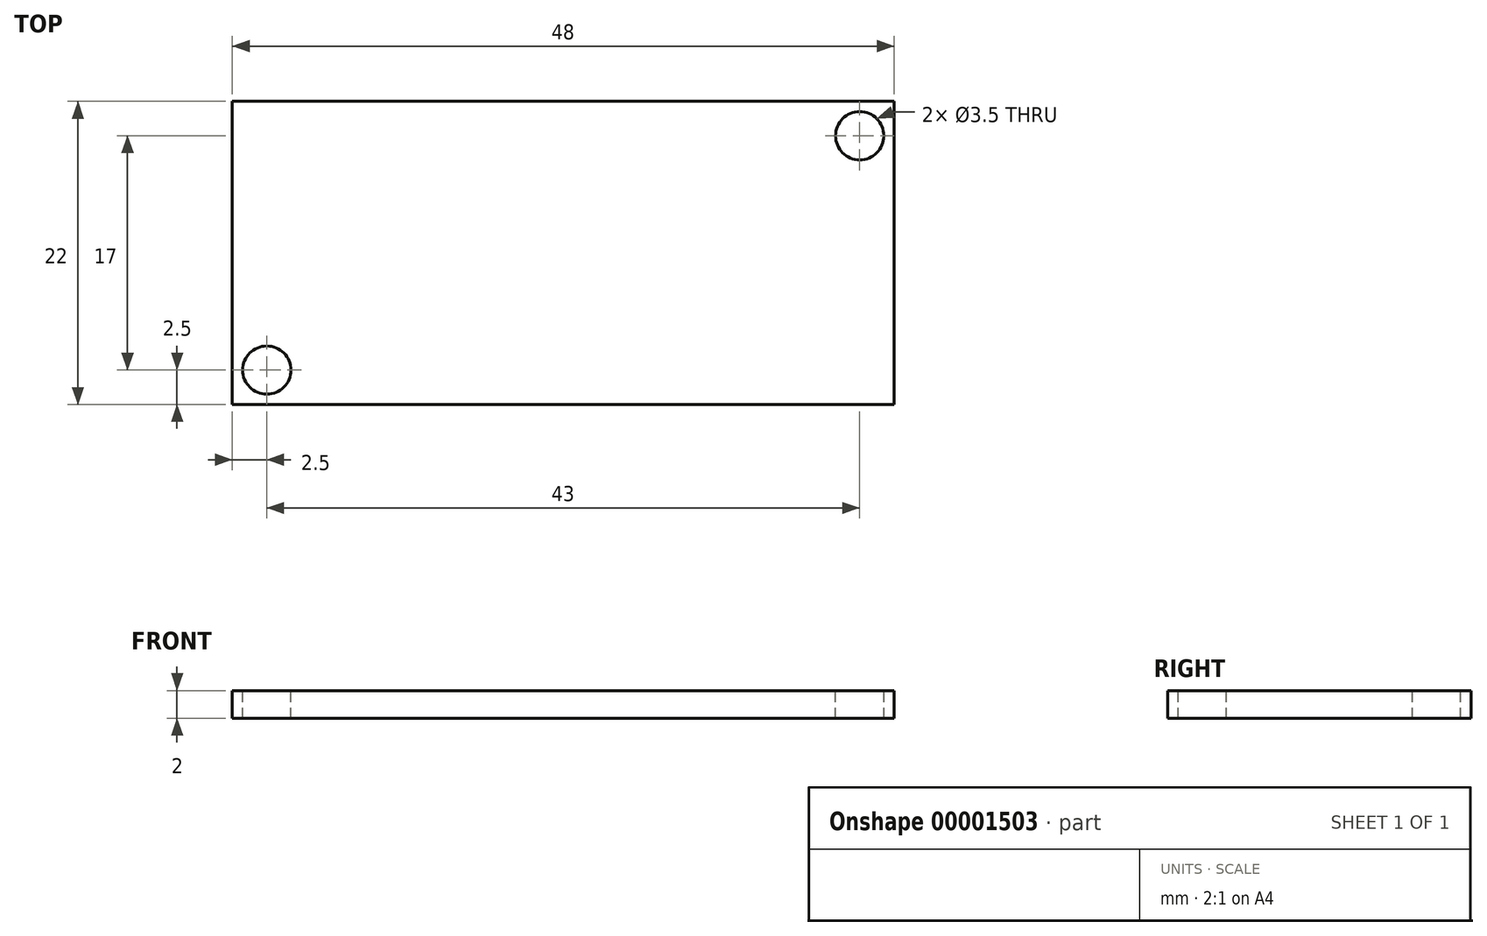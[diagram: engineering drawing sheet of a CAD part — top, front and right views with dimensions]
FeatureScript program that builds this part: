
annotation { "Feature Type Name" : "Feature", "Feature Type Description" : "" }
export const myFeature = defineFeature(function(context is Context, id is Id, definition is map)
    precondition{}
    {
        {
            var Q0;
            Q0=qCreatedBy(makeId("Top.planeOp"),FACE);
            var sketch = newSketch(context, id + "F0", { "sketchPlane" : qUnion([Q0])});
            skLineSegment(sketch, "E0.bottom", {"start": v(0, 0) * mm, "end": v(48, 0) * mm});
            skLineSegment(sketch, "E0.top", {"start": v(0, 22) * mm, "end": v(48, 22) * mm});
            skLineSegment(sketch, "E0.left", {"start": v(0, 0) * mm, "end": v(0, 22) * mm});
            skLineSegment(sketch, "E0.right", {"start": v(48, 0) * mm, "end": v(48, 22) * mm});
            skSolve(sketch);
        }
        {
            var Q0;
            Q0=makeQuery(id+"F0.imprint","IMPRINT",FACE,{"disambiguationData":[TD([[makeQuery(id+"F0.imprint","IMPRINT",EDGE,{"derivedFrom":sQuery(id+"F0.wireOp",EDGE,"E0.bottom")}),1.0]])]});
            extrude(context, id + "F1", {"entities" : qUnion([Q0]), "depth" : 2 * mm});
        }
        {
            var Q0;
            Q0=makeQuery(id+"F1.opExtrude","CAP_FACE",FACE,{"disambiguationData":[OSD([sQuery(id+"F0.wireOp",EDGE,"E0.bottom"),sQuery(id+"F0.wireOp",EDGE,"E0.top"),sQuery(id+"F0.wireOp",EDGE,"E0.left"),sQuery(id+"F0.wireOp",EDGE,"E0.right")])],"isStart":false});
            var sketch = newSketch(context, id + "F2", { "sketchPlane" : qUnion([Q0])});
            skCircle(sketch, "E1", {"center": v(2.5, 2.5) * mm, "radius": 1.75 * mm});
            skCircle(sketch, "E2", {"center": v(45.5, 19.5) * mm, "radius": 1.75 * mm});
            skSolve(sketch);
        }
        {
            var Q0;
            Q0 = qSketchRegion(id + "F2", true);
            extrude(context, id + "F3", {"entities" : qUnion([Q0]), "operationType" : NewBodyOperationType.REMOVE, "oppositeDirection" : true, "depth" : 6.74 * mm});
        }
    });
